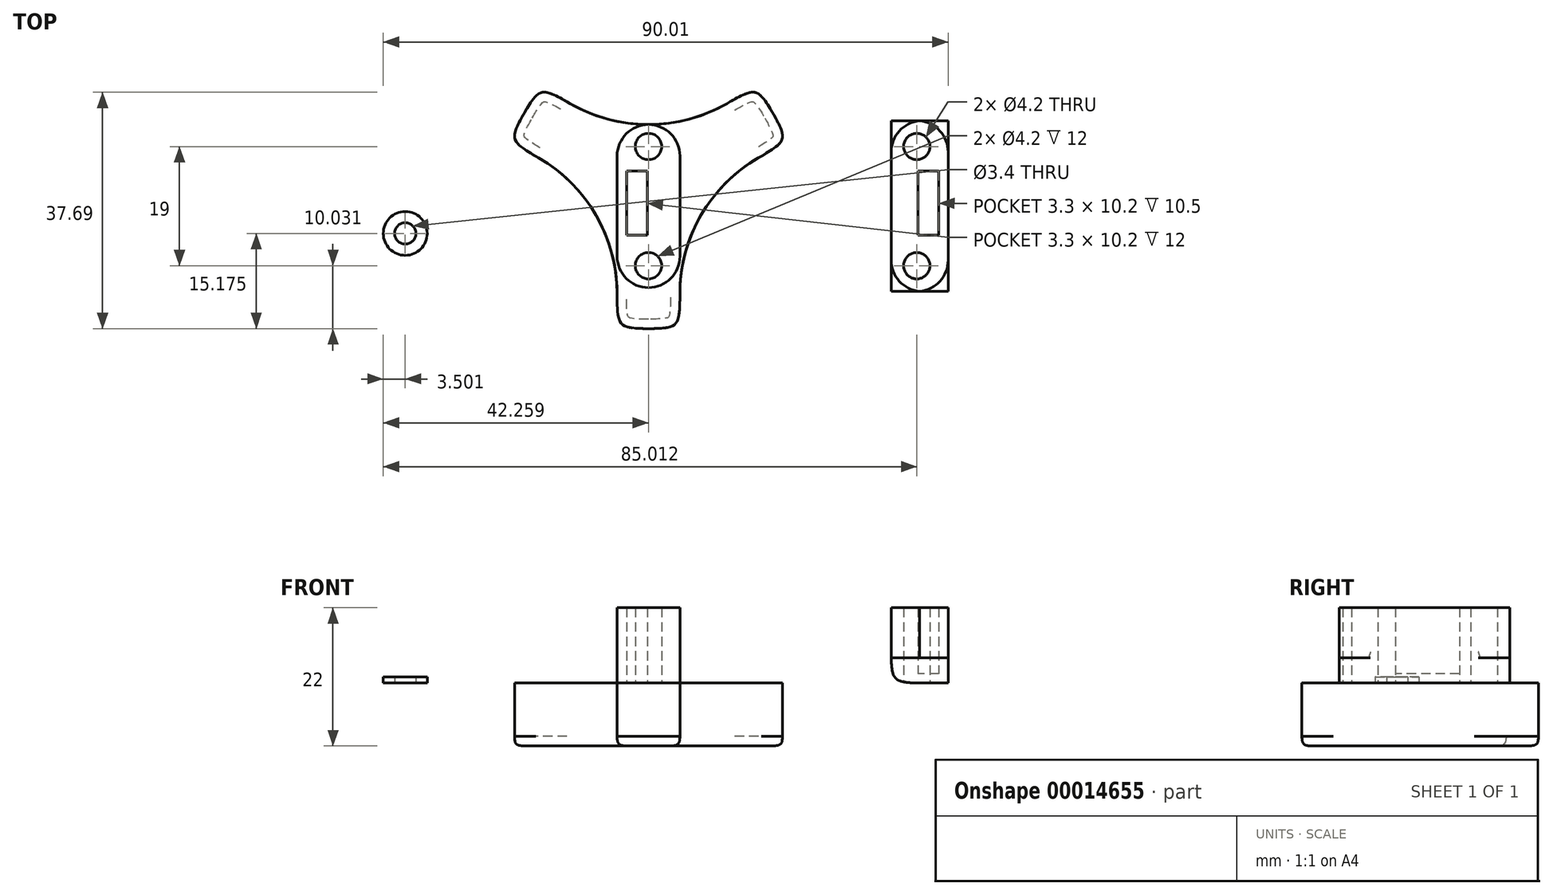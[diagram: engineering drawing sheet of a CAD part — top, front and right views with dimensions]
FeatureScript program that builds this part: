
annotation { "Feature Type Name" : "Feature", "Feature Type Description" : "" }
export const myFeature = defineFeature(function(context is Context, id is Id, definition is map)
    precondition{}
    {
        {
            var Q0;
            Q0=qCreatedBy(makeId("Top.planeOp"),FACE);
            var sketch = newSketch(context, id + "F0", { "sketchPlane" : qUnion([Q0])});
            skLineSegment(sketch, "E0.bottom", {"start": v(-1.4, -6.47) * mm, "end": v(8.6, -6.47) * mm});
            skLineSegment(sketch, "E0.top", {"start": v(-1.4, -26.47) * mm, "end": v(8.6, -26.47) * mm});
            skLineSegment(sketch, "E0.left", {"start": v(-1.4, -6.47) * mm, "end": v(-1.4, -26.47) * mm});
            skLineSegment(sketch, "E0.right", {"start": v(8.6, -6.47) * mm, "end": v(8.6, -26.47) * mm});
            skLineSegment(sketch, "E1", {"start": v(3.6, -26.47) * mm, "end": v(3.6, 13.87) * mm, "construction": true});
            skPoint(sketch, "E2", {"position": v(3.6, -3.58) * mm});
            skLineSegment(sketch, "E3", {"start": v(-1.4, -6.47) * mm, "end": v(3.6, -3.58) * mm});
            skLineSegment(sketch, "E4", {"start": v(8.6, -6.47) * mm, "end": v(3.6, -3.58) * mm});
            skLineSegment(sketch, "E5.1.0", {"start": v(3.6, 2.2) * mm, "end": v(3.6, -3.58) * mm});
            skLineSegment(sketch, "E5.1.1", {"start": v(8.6, -6.47) * mm, "end": v(25.92, 3.53) * mm});
            skLineSegment(sketch, "E5.1.4", {"start": v(8.6, -6.47) * mm, "end": v(3.6, 2.2) * mm});
            skLineSegment(sketch, "E5.1.5", {"start": v(25.92, 3.53) * mm, "end": v(20.92, 12.2) * mm});
            skLineSegment(sketch, "E5.1.6", {"start": v(3.6, 2.2) * mm, "end": v(20.92, 12.2) * mm});
            skLineSegment(sketch, "E5.2.1", {"start": v(3.6, 2.2) * mm, "end": v(-13.72, 12.2) * mm});
            skLineSegment(sketch, "E5.2.2", {"start": v(3.6, 2.2) * mm, "end": v(3.6, -3.58) * mm});
            skLineSegment(sketch, "E5.2.4", {"start": v(3.6, 2.2) * mm, "end": v(-1.4, -6.47) * mm});
            skLineSegment(sketch, "E5.2.5", {"start": v(-13.72, 12.2) * mm, "end": v(-18.72, 3.53) * mm});
            skLineSegment(sketch, "E5.2.6", {"start": v(-1.4, -6.47) * mm, "end": v(-18.72, 3.53) * mm});
            skPoint(sketch, "E6", {"position": v(3.6, -7.8) * mm});
            skSolve(sketch);
        }
        {
            var Q0;
            Q0 = qSketchRegion(id + "F0", true);
            extrude(context, id + "F1", {"entities" : qUnion([Q0]), "oppositeDirection" : true, "depth" : 10 * mm});
        }
        {
            var Q0;
            Q0=makeQuery(id+"F1.opExtrude","SWEPT_EDGE",EDGE,{"disambiguationData":[OSD([sQuery(id+"F0.wireOp",EDGE,"E5.2.1"),sQuery(id+"F0.wireOp",EDGE,"E5.2.5")])]});
            var Q1;
            Q1=makeQuery(id+"F1.opExtrude","SWEPT_EDGE",EDGE,{"disambiguationData":[OSD([sQuery(id+"F0.wireOp",EDGE,"E5.2.5"),sQuery(id+"F0.wireOp",EDGE,"E5.2.6")])]});
            var Q2;
            Q2=makeQuery(id+"F1.opExtrude","SWEPT_EDGE",EDGE,{"disambiguationData":[OSD([sQuery(id+"F0.wireOp",EDGE,"E5.1.5"),sQuery(id+"F0.wireOp",EDGE,"E5.1.6")])]});
            var Q3;
            Q3=makeQuery(id+"F1.opExtrude","SWEPT_EDGE",EDGE,{"disambiguationData":[OSD([sQuery(id+"F0.wireOp",EDGE,"E5.1.1"),sQuery(id+"F0.wireOp",EDGE,"E5.1.5")])]});
            var Q4;
            Q4=makeQuery(id+"F1.opExtrude","SWEPT_EDGE",EDGE,{"disambiguationData":[OSD([sQuery(id+"F0.wireOp",EDGE,"E0.top"),sQuery(id+"F0.wireOp",EDGE,"E0.right")])]});
            var Q5;
            Q5=makeQuery(id+"F1.opExtrude","SWEPT_EDGE",EDGE,{"disambiguationData":[OSD([sQuery(id+"F0.wireOp",EDGE,"E0.top"),sQuery(id+"F0.wireOp",EDGE,"E0.left")])]});
            fillet(context, id + "F2", {"entities" : qUnion([Q0, Q1, Q2, Q3, Q4, Q5]), "radius" : 5 * mm, "tangentPropagation" : true, "rho" : 0.7, "crossSection" : FilletCrossSection.CONIC, "allowEdgeOverflow" : false});
        }
        {
            var Q0;
            Q0=makeQuery(id+"F1.opExtrude","SWEPT_EDGE",EDGE,{"disambiguationData":[OSD([sQuery(id+"F0.wireOp",EDGE,"E0.bottom"),sQuery(id+"F0.wireOp",EDGE,"E0.right"),sQuery(id+"F0.wireOp",EDGE,"E5.1.1"),sQuery(id+"F0.wireOp",EDGE,"E4"),sQuery(id+"F0.wireOp",EDGE,"E5.1.4")])]});
            var Q1;
            Q1=makeQuery(id+"F1.opExtrude","SWEPT_EDGE",EDGE,{"disambiguationData":[OSD([sQuery(id+"F0.wireOp",EDGE,"E0.bottom"),sQuery(id+"F0.wireOp",EDGE,"E0.left"),sQuery(id+"F0.wireOp",EDGE,"E3"),sQuery(id+"F0.wireOp",EDGE,"E5.2.4"),sQuery(id+"F0.wireOp",EDGE,"E5.2.6")])]});
            var Q2;
            Q2=makeQuery(id+"F1.opExtrude","SWEPT_EDGE",EDGE,{"disambiguationData":[OSD([sQuery(id+"F0.wireOp",EDGE,"E5.1.4"),sQuery(id+"F0.wireOp",EDGE,"E5.1.6"),sQuery(id+"F0.wireOp",EDGE,"E5.2.1"),sQuery(id+"F0.wireOp",EDGE,"E5.2.2"),sQuery(id+"F0.wireOp",EDGE,"E5.2.4")])]});
            fillet(context, id + "F3", {"entities" : qUnion([Q0, Q1, Q2]), "radius" : 25 * mm, "allowEdgeOverflow" : false});
        }
        {
            var Q0;
            Q0=qCreatedBy(makeId("Top.planeOp"),FACE);
            var sketch = newSketch(context, id + "F4", { "sketchPlane" : qUnion([Q0])});
            skLineSegment(sketch, "E7.bottom", {"start": v(-1.4, 6.06) * mm, "end": v(8.6, 6.06) * mm});
            skLineSegment(sketch, "E7.top", {"start": v(-1.4, -19.94) * mm, "end": v(8.6, -19.94) * mm});
            skLineSegment(sketch, "E7.left", {"start": v(-1.4, 6.06) * mm, "end": v(-1.4, -19.94) * mm});
            skLineSegment(sketch, "E7.right", {"start": v(8.6, 6.06) * mm, "end": v(8.6, -19.94) * mm});
            skLineSegment(sketch, "E8", {"start": v(3.6, 6.06) * mm, "end": v(3.6, -19.94) * mm, "construction": true});
            skLineSegment(sketch, "E9.bottom", {"start": v(0.1, -1.37) * mm, "end": v(3.4, -1.37) * mm});
            skLineSegment(sketch, "E9.top", {"start": v(0.1, -11.57) * mm, "end": v(3.4, -11.57) * mm});
            skLineSegment(sketch, "E9.left", {"start": v(0.1, -1.37) * mm, "end": v(0.1, -11.57) * mm});
            skLineSegment(sketch, "E9.right", {"start": v(3.4, -1.37) * mm, "end": v(3.4, -11.57) * mm});
            skCircle(sketch, "E10", {"center": v(3.6, 2.56) * mm, "radius": 2.1 * mm});
            skCircle(sketch, "E11", {"center": v(3.6, -16.44) * mm, "radius": 2.1 * mm});
            skLineSegment(sketch, "E12", {"start": v(-1.4, -6.94) * mm, "end": v(8.6, -6.94) * mm, "construction": true});
            skPoint(sketch, "E13", {"position": v(0.1, -6.47) * mm});
            skLineSegment(sketch, "E14", {"start": v(24.98, 11.89) * mm, "end": v(24.98, -28.7) * mm, "construction": true});
            skLineSegment(sketch, "E15.MirrorCS", {"start": v(51.35, 6.06) * mm, "end": v(51.35, -19.94) * mm});
            skCircle(sketch, "E16.MirrorC", {"center": v(46.35, 2.56) * mm, "radius": 2.1 * mm});
            skLineSegment(sketch, "E17.MirrorCS", {"start": v(49.85, -1.37) * mm, "end": v(49.85, -11.57) * mm});
            skLineSegment(sketch, "E18.MirrorCS", {"start": v(49.85, -1.37) * mm, "end": v(46.55, -1.37) * mm});
            skLineSegment(sketch, "E19.MirrorCS", {"start": v(46.55, -1.37) * mm, "end": v(46.55, -11.57) * mm});
            skLineSegment(sketch, "E20.MirrorCS", {"start": v(49.85, -11.57) * mm, "end": v(46.55, -11.57) * mm});
            skCircle(sketch, "E21.MirrorC", {"center": v(46.35, -16.44) * mm, "radius": 2.1 * mm});
            skLineSegment(sketch, "E22", {"start": v(51.35, 6.06) * mm, "end": v(51.35, 6.66) * mm});
            skLineSegment(sketch, "E23", {"start": v(51.35, 6.66) * mm, "end": v(42.25, 6.66) * mm});
            skLineSegment(sketch, "E24", {"start": v(42.25, 6.66) * mm, "end": v(42.25, -20.54) * mm});
            skLineSegment(sketch, "E25", {"start": v(42.25, -20.54) * mm, "end": v(51.35, -20.54) * mm});
            skLineSegment(sketch, "E26", {"start": v(51.35, -20.54) * mm, "end": v(51.35, -19.94) * mm});
            skSolve(sketch);
        }
        {
            var Q0;
            Q0=makeQuery(id+"F4.imprint","IMPRINT",FACE,{"disambiguationData":[TD([[makeQuery(id+"F4.imprint","IMPRINT",EDGE,{"derivedFrom":sQuery(id+"F4.wireOp",EDGE,"E7.bottom")}),-1.0]])]});
            extrude(context, id + "F5", {"entities" : qUnion([Q0]), "operationType" : NewBodyOperationType.ADD, "depth" : 12 * mm});
        }
        {
            var Q0;
            Q0=makeQuery(id+"F4.imprint","IMPRINT",FACE,{"disambiguationData":[TD([[makeQuery(id+"F4.imprint","IMPRINT",EDGE,{"derivedFrom":sQuery(id+"F4.wireOp",EDGE,"E15.MirrorCS")}),-1.0]])]});
            extrude(context, id + "F6", {"entities" : qUnion([Q0]), "depth" : 12 * mm});
        }
        {
            var Q0;
            Q0=makeQuery(id+"F4.imprint","IMPRINT",FACE,{"disambiguationData":[TD([[makeQuery(id+"F4.imprint","IMPRINT",EDGE,{"derivedFrom":sQuery(id+"F4.wireOp",EDGE,"E15.MirrorCS")}),-1.0]])]});
            var Q1;
            Q1=makeQuery(id+"F4.imprint","IMPRINT",FACE,{"disambiguationData":[TD([[makeQuery(id+"F4.imprint","IMPRINT",EDGE,{"derivedFrom":sQuery(id+"F4.wireOp",EDGE,"E16.MirrorC")}),-1.0]])]});
            var Q2;
            Q2=makeQuery(id+"F4.imprint","IMPRINT",FACE,{"disambiguationData":[TD([[makeQuery(id+"F4.imprint","IMPRINT",EDGE,{"derivedFrom":sQuery(id+"F4.wireOp",EDGE,"E17.MirrorCS")}),-1.0]])]});
            var Q3;
            Q3=makeQuery(id+"F4.imprint","IMPRINT",FACE,{"disambiguationData":[TD([[makeQuery(id+"F4.imprint","IMPRINT",EDGE,{"derivedFrom":sQuery(id+"F4.wireOp",EDGE,"E21.MirrorC")}),-1.0]])]});
            extrude(context, id + "F7", {"entities" : qUnion([Q0, Q1, Q2, Q3]), "operationType" : NewBodyOperationType.ADD, "depth" : 1.5 * mm});
        }
        {
            var Q0;
            Q0=qCreatedBy(makeId("Top.planeOp"),FACE);
            var sketch = newSketch(context, id + "F8", { "sketchPlane" : qUnion([Q0])});
            skCircle(sketch, "E27", {"center": v(-35.16, -11.3) * mm, "radius": 3.5 * mm});
            skCircle(sketch, "E28", {"center": v(-35.16, -11.3) * mm, "radius": 1.7 * mm});
            skLineSegment(sketch, "E29", {"start": v(-46.83, -11.3) * mm, "end": v(-19.95, -11.3) * mm, "construction": true});
            skPoint(sketch, "E30", {"position": v(-38.66, -11.3) * mm});
            skPoint(sketch, "E31", {"position": v(-31.66, -11.3) * mm});
            skSolve(sketch);
        }
        {
            var Q0;
            Q0=makeQuery(id+"F8.imprint","IMPRINT",FACE,{"disambiguationData":[TD([[makeQuery(id+"F8.imprint","IMPRINT",EDGE,{"derivedFrom":sQuery(id+"F8.wireOp",EDGE,"E27")}),1.0]])]});
            extrude(context, id + "F9", {"entities" : qUnion([Q0]), "depth" : 1 * mm});
        }
        {
            var Q0;
            Q0=makeQuery(id+"F5.opExtrude","SWEPT_EDGE",EDGE,{"disambiguationData":[OSD([sQuery(id+"F4.wireOp",EDGE,"E7.top"),sQuery(id+"F4.wireOp",EDGE,"E7.left")])]});
            var Q1;
            Q1=makeQuery(id+"F5.opExtrude","SWEPT_EDGE",EDGE,{"disambiguationData":[OSD([sQuery(id+"F4.wireOp",EDGE,"E7.top"),sQuery(id+"F4.wireOp",EDGE,"E7.right")])]});
            var Q2;
            Q2=makeQuery(id+"F5.opExtrude","SWEPT_EDGE",EDGE,{"disambiguationData":[OSD([sQuery(id+"F4.wireOp",EDGE,"E7.bottom"),sQuery(id+"F4.wireOp",EDGE,"E7.left")])]});
            var Q3;
            Q3=makeQuery(id+"F5.opExtrude","SWEPT_EDGE",EDGE,{"disambiguationData":[OSD([sQuery(id+"F4.wireOp",EDGE,"E7.bottom"),sQuery(id+"F4.wireOp",EDGE,"E7.right")])]});
            var Q4;
            Q4=makeQuery(id+"F6.opExtrude","SWEPT_EDGE",EDGE,{"disambiguationData":[OSD([sQuery(id+"F4.wireOp",EDGE,"E24"),sQuery(id+"F4.wireOp",EDGE,"E25")])]});
            var Q5;
            Q5=makeQuery(id+"F6.opExtrude","SWEPT_EDGE",EDGE,{"disambiguationData":[OSD([sQuery(id+"F4.wireOp",EDGE,"E25"),sQuery(id+"F4.wireOp",EDGE,"E26")])]});
            var Q6;
            Q6=makeQuery(id+"F6.opExtrude","SWEPT_EDGE",EDGE,{"disambiguationData":[OSD([sQuery(id+"F4.wireOp",EDGE,"E23"),sQuery(id+"F4.wireOp",EDGE,"E24")])]});
            var Q7;
            Q7=makeQuery(id+"F6.opExtrude","SWEPT_EDGE",EDGE,{"disambiguationData":[OSD([sQuery(id+"F4.wireOp",EDGE,"E22"),sQuery(id+"F4.wireOp",EDGE,"E23")])]});
            fillet(context, id + "F10", {"entities" : qUnion([Q0, Q1, Q2, Q3, Q4, Q5, Q6, Q7]), "radius" : 5 * mm, "tangentPropagation" : true, "allowEdgeOverflow" : false});
        }
        {
            var Q0;
            Q0=makeQuery(id+"F4.imprint","IMPRINT",FACE,{"disambiguationData":[TD([[makeQuery(id+"F4.imprint","IMPRINT",EDGE,{"derivedFrom":sQuery(id+"F4.wireOp",EDGE,"E16.MirrorC")}),-1.0]])]});
            var Q1;
            Q1=makeQuery(id+"F4.imprint","IMPRINT",FACE,{"disambiguationData":[TD([[makeQuery(id+"F4.imprint","IMPRINT",EDGE,{"derivedFrom":sQuery(id+"F4.wireOp",EDGE,"E21.MirrorC")}),-1.0]])]});
            extrude(context, id + "F11", {"entities" : qUnion([Q0, Q1]), "operationType" : NewBodyOperationType.ADD, "depth" : 4 * mm});
        }
        {
            var Q0;
            Q0=makeQuery(id+"F6.opExtrude","CAP_EDGE",EDGE,{"disambiguationData":[OSD([sQuery(id+"F4.wireOp",EDGE,"E24")])],"isStart":true});
            var Q1;
            {var subQ0=sQuery(id+"F4.wireOp",EDGE,"E23");var subQ1=sQuery(id+"F4.wireOp",EDGE,"E24");var subQ2=sQuery(id+"F4.wireOp",EDGE,"E15.MirrorCS");var subQ3=sQuery(id+"F4.wireOp",EDGE,"E22");var subQ4=sQuery(id+"F4.wireOp",EDGE,"E25");var subQ5=sQuery(id+"F4.wireOp",EDGE,"E26");Q1=makeQuery(id+"F10.opFillet","BLEND_EDGE",EDGE,{"blendedFrom":[makeQuery(id+"F6.opExtrude","SWEPT_EDGE",EDGE,{"disambiguationData":[OSD([subQ0,subQ1])]}),makeQuery(id+"F7.boolean.opBoolean","MERGE",FACE,{"derivedFrom":[makeQuery(id+"F6.opExtrude","CAP_FACE",FACE,{"disambiguationData":[OSD([subQ2,sQuery(id+"F4.wireOp",EDGE,"E16.MirrorC"),sQuery(id+"F4.wireOp",EDGE,"E17.MirrorCS"),sQuery(id+"F4.wireOp",EDGE,"E18.MirrorCS"),sQuery(id+"F4.wireOp",EDGE,"E19.MirrorCS"),sQuery(id+"F4.wireOp",EDGE,"E20.MirrorCS"),sQuery(id+"F4.wireOp",EDGE,"E21.MirrorC"),subQ3,subQ0,subQ1,subQ4,subQ5])],"isStart":true}),makeQuery(id+"F7.opExtrude","CAP_FACE",FACE,{"disambiguationData":[OSD([subQ2,subQ3,subQ0,subQ1,subQ4,subQ5])],"isStart":true})]})],"blendedInto":[makeQuery(id+"F7.boolean.opBoolean","MERGE",FACE,{"derivedFrom":[makeQuery(id+"F6.opExtrude","CAP_FACE",FACE,{"disambiguationData":[OSD([subQ2,sQuery(id+"F4.wireOp",EDGE,"E16.MirrorC"),sQuery(id+"F4.wireOp",EDGE,"E17.MirrorCS"),sQuery(id+"F4.wireOp",EDGE,"E18.MirrorCS"),sQuery(id+"F4.wireOp",EDGE,"E19.MirrorCS"),sQuery(id+"F4.wireOp",EDGE,"E20.MirrorCS"),sQuery(id+"F4.wireOp",EDGE,"E21.MirrorC"),subQ3,subQ0,subQ1,subQ4,subQ5])],"isStart":true}),makeQuery(id+"F7.opExtrude","CAP_FACE",FACE,{"disambiguationData":[OSD([subQ2,subQ3,subQ0,subQ1,subQ4,subQ5])],"isStart":true})]})]});}
            var Q2;
            {var subQ0=sQuery(id+"F4.wireOp",EDGE,"E24");var subQ1=sQuery(id+"F4.wireOp",EDGE,"E25");var subQ2=sQuery(id+"F4.wireOp",EDGE,"E15.MirrorCS");var subQ3=sQuery(id+"F4.wireOp",EDGE,"E22");var subQ4=sQuery(id+"F4.wireOp",EDGE,"E23");var subQ5=sQuery(id+"F4.wireOp",EDGE,"E26");Q2=makeQuery(id+"F10.opFillet","BLEND_EDGE",EDGE,{"blendedFrom":[makeQuery(id+"F6.opExtrude","SWEPT_EDGE",EDGE,{"disambiguationData":[OSD([subQ0,subQ1])]}),makeQuery(id+"F7.boolean.opBoolean","MERGE",FACE,{"derivedFrom":[makeQuery(id+"F6.opExtrude","CAP_FACE",FACE,{"disambiguationData":[OSD([subQ2,sQuery(id+"F4.wireOp",EDGE,"E16.MirrorC"),sQuery(id+"F4.wireOp",EDGE,"E17.MirrorCS"),sQuery(id+"F4.wireOp",EDGE,"E18.MirrorCS"),sQuery(id+"F4.wireOp",EDGE,"E19.MirrorCS"),sQuery(id+"F4.wireOp",EDGE,"E20.MirrorCS"),sQuery(id+"F4.wireOp",EDGE,"E21.MirrorC"),subQ3,subQ4,subQ0,subQ1,subQ5])],"isStart":true}),makeQuery(id+"F7.opExtrude","CAP_FACE",FACE,{"disambiguationData":[OSD([subQ2,subQ3,subQ4,subQ0,subQ1,subQ5])],"isStart":true})]})],"blendedInto":[makeQuery(id+"F7.boolean.opBoolean","MERGE",FACE,{"derivedFrom":[makeQuery(id+"F6.opExtrude","CAP_FACE",FACE,{"disambiguationData":[OSD([subQ2,sQuery(id+"F4.wireOp",EDGE,"E16.MirrorC"),sQuery(id+"F4.wireOp",EDGE,"E17.MirrorCS"),sQuery(id+"F4.wireOp",EDGE,"E18.MirrorCS"),sQuery(id+"F4.wireOp",EDGE,"E19.MirrorCS"),sQuery(id+"F4.wireOp",EDGE,"E20.MirrorCS"),sQuery(id+"F4.wireOp",EDGE,"E21.MirrorC"),subQ3,subQ4,subQ0,subQ1,subQ5])],"isStart":true}),makeQuery(id+"F7.opExtrude","CAP_FACE",FACE,{"disambiguationData":[OSD([subQ2,subQ3,subQ4,subQ0,subQ1,subQ5])],"isStart":true})]})]});}
            fillet(context, id + "F12", {"entities" : qUnion([Q0, Q1, Q2]), "radius" : 5 * mm, "tangentPropagation" : true, "rho" : 0.7, "crossSection" : FilletCrossSection.CONIC, "allowEdgeOverflow" : false});
        }
        {
            var Q0;
            Q0=makeQuery(id+"F1.opExtrude","CAP_FACE",FACE,{"disambiguationData":[OSD([sQuery(id+"F0.wireOp",EDGE,"E0.top"),sQuery(id+"F0.wireOp",EDGE,"E0.left"),sQuery(id+"F0.wireOp",EDGE,"E0.right"),sQuery(id+"F0.wireOp",EDGE,"E5.1.1"),sQuery(id+"F0.wireOp",EDGE,"E5.1.5"),sQuery(id+"F0.wireOp",EDGE,"E5.1.6"),sQuery(id+"F0.wireOp",EDGE,"E5.2.1"),sQuery(id+"F0.wireOp",EDGE,"E5.2.5"),sQuery(id+"F0.wireOp",EDGE,"E5.2.6")])],"isStart":false});
            fillet(context, id + "F13", {"entities" : qUnion([Q0]), "radius" : 1.5 * mm, "tangentPropagation" : true, "rho" : 0.6, "crossSection" : FilletCrossSection.CONIC, "allowEdgeOverflow" : false});
        }
    });
